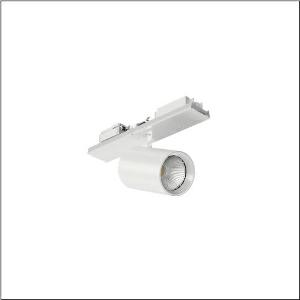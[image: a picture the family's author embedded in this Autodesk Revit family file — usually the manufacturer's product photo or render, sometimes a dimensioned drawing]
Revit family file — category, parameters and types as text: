
# Revit family: licross_r__spot_31_51sl12da45b_e1b3
name_source: partatom
category: Lighting Fixtures
units: mm (PartAtom-declared; Revit-internal decimal feet)

## family parameters
Cut with Voids When Loaded = No
Host = Face
Light Source = No
Part Type = Normal
Room Calculation Point = No
Round Connector Dimension = Use Diameter
Shared = No

## types (1)
- --- (1 x LED, 5140 lm, 43.9 W, 4000K)
    Apparent Load = 44 VA
    CIE Flux Codes = 93 97 99 100 100
    Color Rendering = 90
    Color Temperature = 4000K
    Default Elevation = 1800 mm
    Description = Licross® Spot 31, directional spotlight, light control with lens, of plastic, LED rated luminous flux: 5.140lm, light colour: 940, with plug, 5-pole, mains connection: 220..240V, AC, 50/60Hz, of aluminium, traffic white (RAL 9016), length: 300mm, diameter: 90mm, protection rating (complete): IP20, insulation class (complete): insulation class I (protective earthing), certification: CE, packaging unit: 1 piece
    Height = 175 mm
    Lamp = 1 x LED
    Lamp Light Flux = 5140 lm
    Lamp Power = 43.9 W
    Lamp count = 1
    Length = 90 mm
    Luminous efficacy = 117 lm/W
    Manufacturer = Siteco
    ModVariant = No
    Model = 51SL12DA45B
    Mounting Place = Ceiling
    Mounting Type = Pendant
    Number of Poles = 1
    OnlyDefault = Yes
    Power Factor = 1
    Product Name = Licross® Spot 31
    Product group = directional spotlight
    ProductGroupID = 906
    Protection Class = Protection class I
    Protection Degree = IP 20
    RLX_Detail_Level = 1
    RLX_Emergency_Light_Flux = 0 lm
    RLX_Emergency_Type = 0
    RLX_Emergency_Type_DB = No
    RlxData = <blob elided: 14817 chars, md5=06594801>
    Socket = socket
    Standby Power = 0 W
    System Light Flux = 5140 lm
    System Power = 44 W
    Type Comments = factory setting: luminous flux: 100 % | (ON | ON | ON) | 1050 mA
    Type Image = l_1245720.jpg
    URL = http://relux.com
    VarID = @adj_127826
    Voltage = 0 V
    Weight = 0.00 kg
    Width = 0 mm  [stored 0 ft]

note: [stored X ft] marks values corroborated as IEEE doubles in the binary element streams (Revit-internal decimal feet)

## geometry (parser evidence)
native form markers: Sweep x11
no freeform markers — native parametric forms only
